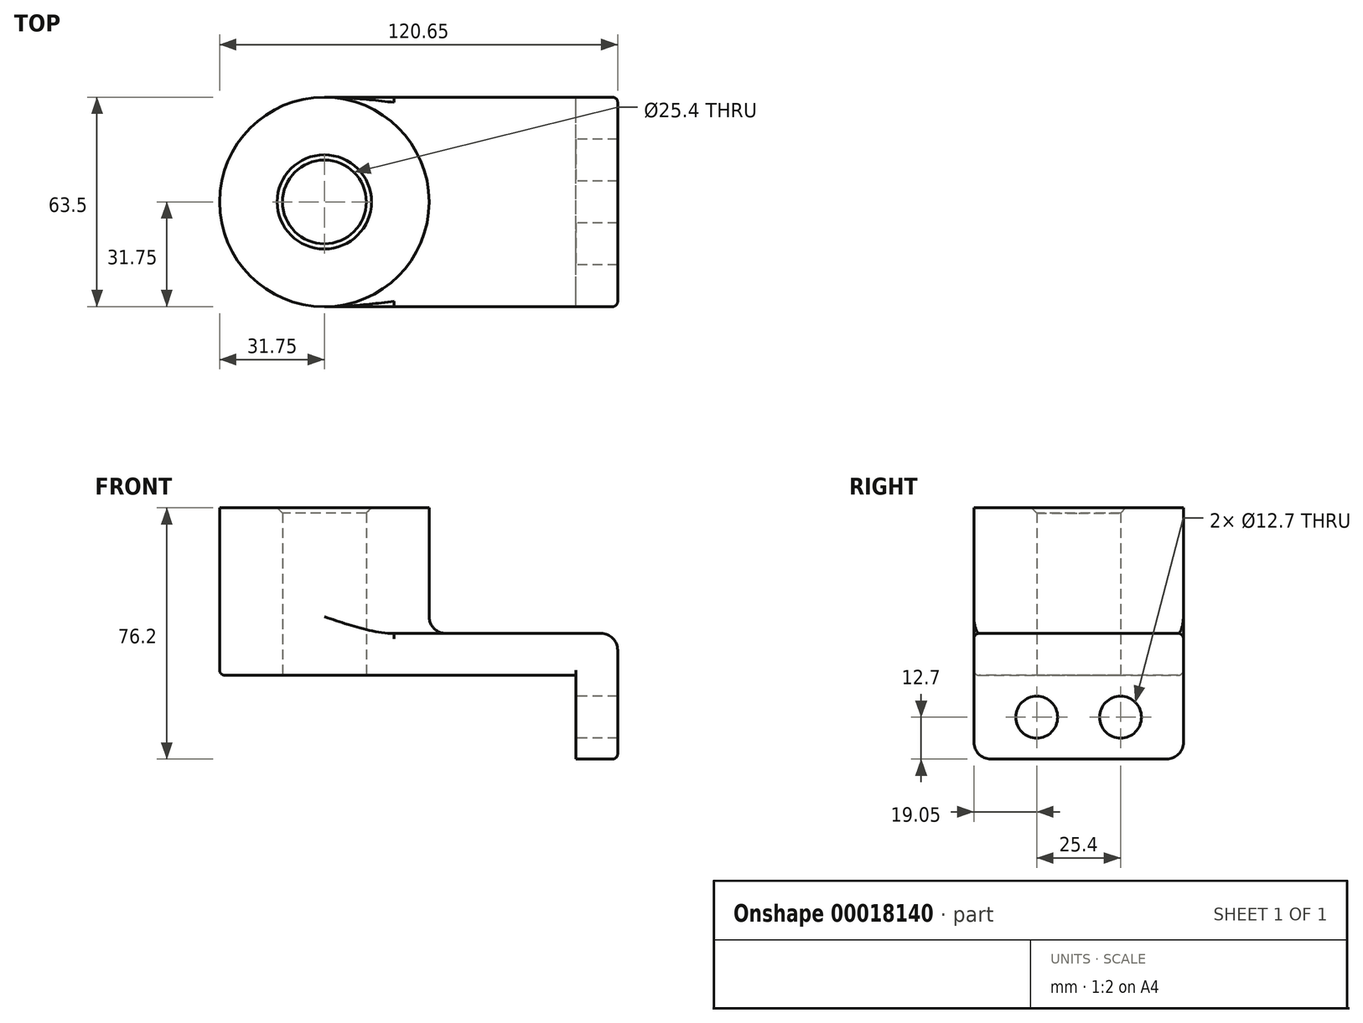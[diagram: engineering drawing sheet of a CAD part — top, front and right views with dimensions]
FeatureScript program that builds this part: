
annotation { "Feature Type Name" : "Feature", "Feature Type Description" : "" }
export const myFeature = defineFeature(function(context is Context, id is Id, definition is map)
    precondition{}
    {
        {
            var Q0;
            Q0=qCreatedBy(makeId("Top.planeOp"),FACE);
            var sketch = newSketch(context, id + "F0", { "sketchPlane" : qUnion([Q0])});
            skLineSegment(sketch, "E0.rect.bottom", {"start": v(38.1, -31.75) * mm, "end": v(-38.1, -31.75) * mm});
            skLineSegment(sketch, "E0.rect.top", {"start": v(38.1, 31.75) * mm, "end": v(-38.1, 31.75) * mm});
            skLineSegment(sketch, "E0.rect.left", {"start": v(38.1, -31.75) * mm, "end": v(38.1, 31.75) * mm});
            skLineSegment(sketch, "E0.rect.right", {"start": v(-38.1, -31.75) * mm, "end": v(-38.1, 31.75) * mm});
            skPoint(sketch, "E0.rect.middle", {"position": v(0, 0) * mm});
            skCircle(sketch, "E1", {"center": v(-38.1, 0) * mm, "radius": 31.75 * mm});
            skCircle(sketch, "E2", {"center": v(-38.1, 0) * mm, "radius": 12.7 * mm});
            skSolve(sketch);
        }
        {
            var Q0;
            Q0 = qSketchRegion(id + "F0", true);
            extrude(context, id + "F1", {"entities" : qUnion([Q0]), "depth" : 12.7 * mm});
        }
        {
            var Q0;
            {var subQ0=sQuery(id+"F0.wireOp",EDGE,"E2");var subQ1=sQuery(id+"F0.wireOp",EDGE,"E0.rect.right");var subQ3=makeQuery(id+"F0.imprint","INTERSECT",VERTEX,{"disambiguationData":[OD(0.0)],"derivedFrom":[subQ1,subQ0]});Q0=makeQuery(id+"F0.imprint","IMPRINT",FACE,{"disambiguationData":[TD([[makeQuery(id+"F0.imprint","IMPRINT",EDGE,{"disambiguationData":[TD([[subQ3,1.0]])],"derivedFrom":subQ0}),-1.0]])]});}
            var Q1;
            {var subQ0=sQuery(id+"F0.wireOp",EDGE,"E2");var subQ1=sQuery(id+"F0.wireOp",EDGE,"E0.rect.right");var subQ3=makeQuery(id+"F0.imprint","INTERSECT",VERTEX,{"disambiguationData":[OD(0.0)],"derivedFrom":[subQ1,subQ0]});Q1=makeQuery(id+"F0.imprint","IMPRINT",FACE,{"disambiguationData":[TD([[makeQuery(id+"F0.imprint","IMPRINT",EDGE,{"disambiguationData":[TD([[subQ3,-1.0]])],"derivedFrom":subQ0}),-1.0]])]});}
            extrude(context, id + "F2", {"entities" : qUnion([Q0, Q1]), "operationType" : NewBodyOperationType.ADD, "depth" : 50.8 * mm});
        }
        {
            var Q0;
            Q0=makeQuery(id+"F1.opExtrude","SWEPT_FACE",FACE,{"disambiguationData":[OSD([sQuery(id+"F0.wireOp",EDGE,"E0.rect.left")])]});
            var sketch = newSketch(context, id + "F3", { "sketchPlane" : qUnion([Q0])});
            skLineSegment(sketch, "E3.bottom", {"start": v(-31.75, 12.7) * mm, "end": v(31.75, 12.7) * mm});
            skLineSegment(sketch, "E3.top", {"start": v(-31.75, -25.4) * mm, "end": v(31.75, -25.4) * mm});
            skLineSegment(sketch, "E3.left", {"start": v(-31.75, 12.7) * mm, "end": v(-31.75, -25.4) * mm});
            skLineSegment(sketch, "E3.right", {"start": v(31.75, 12.7) * mm, "end": v(31.75, -25.4) * mm});
            skCircle(sketch, "E4", {"center": v(-12.7, -12.7) * mm, "radius": 6.35 * mm});
            skLineSegment(sketch, "E5", {"start": v(0, 12.7) * mm, "end": v(0, -25.4) * mm});
            skCircle(sketch, "E6.MirrorC", {"center": v(12.7, -12.7) * mm, "radius": 6.35 * mm});
            skSolve(sketch);
        }
        {
            var Q0;
            Q0 = qSketchRegion(id + "F3", true);
            extrude(context, id + "F4", {"entities" : qUnion([Q0]), "operationType" : NewBodyOperationType.ADD, "depth" : 12.7 * mm});
        }
        {
            var Q0;
            {var subQ0=sQuery(id+"F0.wireOp",EDGE,"E1");Q0=makeQuery(id+"F2.boolean.opBoolean","INTERSECT",EDGE,{"derivedFrom":[makeQuery(id+"F1.opExtrude","CAP_FACE",FACE,{"disambiguationData":[OSD([sQuery(id+"F0.wireOp",EDGE,"E0.rect.bottom"),sQuery(id+"F0.wireOp",EDGE,"E0.rect.top"),sQuery(id+"F0.wireOp",EDGE,"E0.rect.left"),subQ0,sQuery(id+"F0.wireOp",EDGE,"E2")])],"isStart":false}),makeQuery(id+"F2.opExtrude","SWEPT_FACE",FACE,{"disambiguationData":[OSD([subQ0])]})]});}
            var Q1;
            Q1=makeQuery(id+"F4.opExtrude","CAP_EDGE",EDGE,{"disambiguationData":[OSD([sQuery(id+"F3.wireOp",EDGE,"E3.bottom")])],"isStart":false});
            var Q2;
            Q2=makeQuery(id+"F4.opExtrude","SWEPT_EDGE",EDGE,{"disambiguationData":[OSD([sQuery(id+"F3.wireOp",EDGE,"E3.top"),sQuery(id+"F3.wireOp",EDGE,"E3.left")])]});
            var Q3;
            Q3=makeQuery(id+"F4.opExtrude","SWEPT_EDGE",EDGE,{"disambiguationData":[OSD([sQuery(id+"F3.wireOp",EDGE,"E3.top"),sQuery(id+"F3.wireOp",EDGE,"E3.right")])]});
            fillet(context, id + "F5", {"entities" : qUnion([Q0, Q1, Q2, Q3]), "radius" : 5.08 * mm, "tangentPropagation" : true, "allowEdgeOverflow" : false});
        }
        {
            var Q0;
            Q0=makeQuery(id+"F4.boolean.opBoolean","MERGE",EDGE,{"derivedFrom":[makeQuery(id+"F1.opExtrude","CAP_EDGE",EDGE,{"disambiguationData":[OSD([sQuery(id+"F0.wireOp",EDGE,"E0.rect.bottom")])],"isStart":false}),makeQuery(id+"F4.opExtrude","SWEPT_EDGE",EDGE,{"disambiguationData":[OSD([sQuery(id+"F3.wireOp",EDGE,"E3.bottom"),sQuery(id+"F3.wireOp",EDGE,"E3.left")])]})]});
            var Q1;
            Q1=makeQuery(id+"F1.opExtrude","CAP_EDGE",EDGE,{"disambiguationData":[OSD([sQuery(id+"F0.wireOp",EDGE,"E0.rect.bottom")])],"isStart":true});
            var Q2;
            Q2=makeQuery(id+"F1.opExtrude","CAP_EDGE",EDGE,{"disambiguationData":[OSD([sQuery(id+"F0.wireOp",EDGE,"E0.rect.left")])],"isStart":true});
            fillet(context, id + "F6", {"entities" : qUnion([Q0, Q1, Q2]), "radius" : 1.59 * mm, "tangentPropagation" : true, "allowEdgeOverflow" : false});
        }
        {
            var Q0;
            Q0=makeQuery(id+"F2.opExtrude","CAP_EDGE",EDGE,{"disambiguationData":[OSD([sQuery(id+"F0.wireOp",EDGE,"E2")])],"isStart":false});
            chamfer(context, id + "F7", {"entities" : qUnion([Q0]), "width" : 1.59 * mm, "tangentPropagation" : true});
        }
    });
